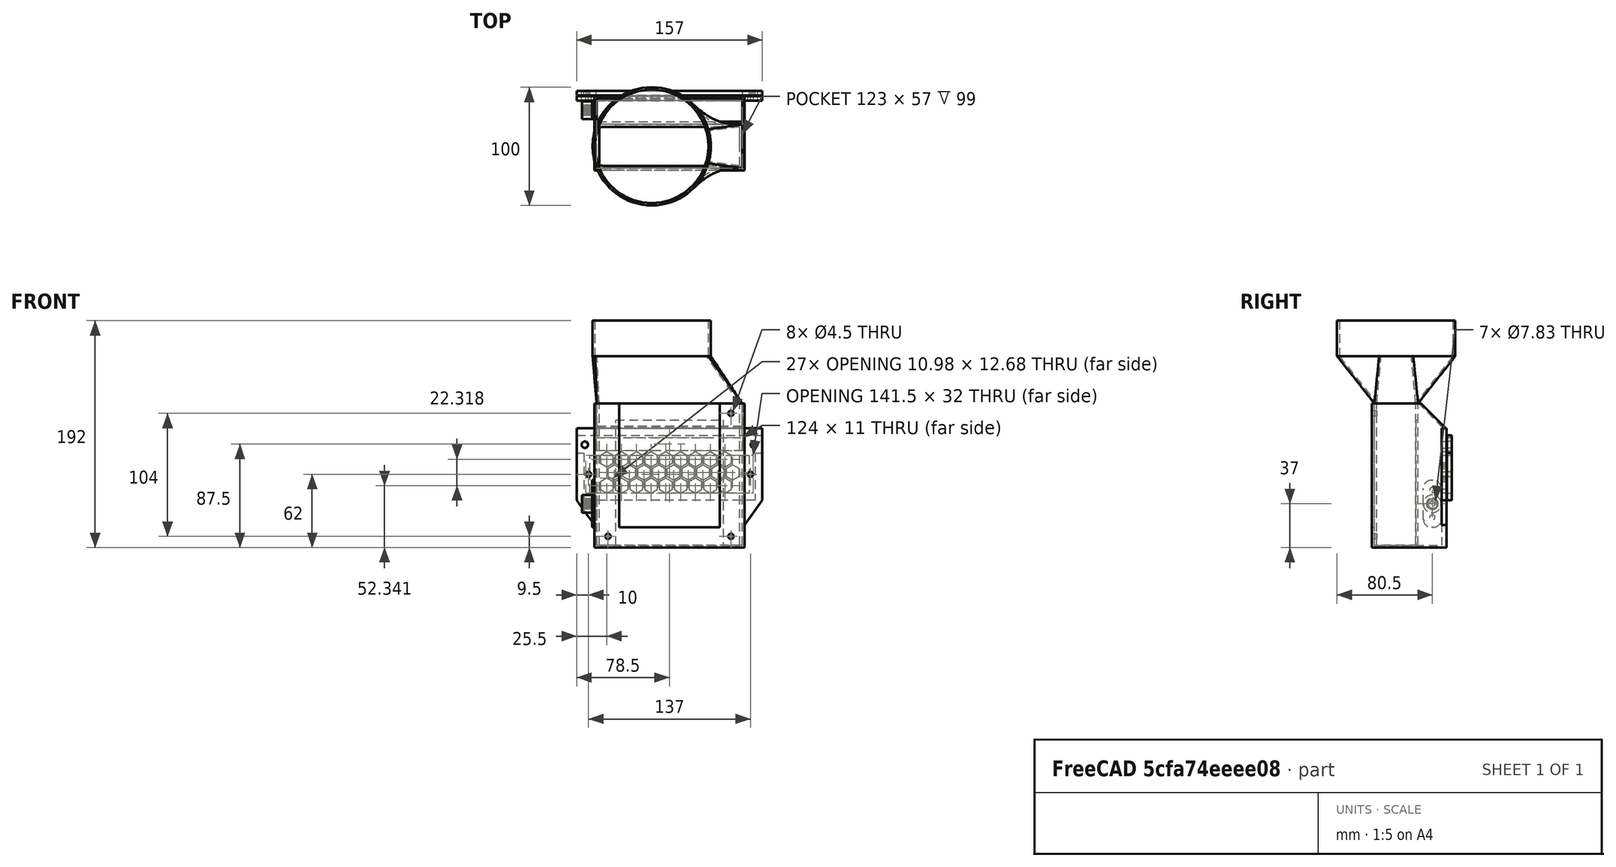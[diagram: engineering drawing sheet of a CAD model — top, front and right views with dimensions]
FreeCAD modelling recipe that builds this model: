
FCSTD DOCUMENT  (FreeCAD 1.0R39109 (Git))
Label: RadialExhaust
License: All rights reserved
LicenseURL: http://en.wikipedia.org/wiki/All_rights_reserved
objects: Sketcher::SketchObject×18, PartDesign::Pad×9, PartDesign::Pocket×8, PartDesign::Body×4, PartDesign::Fillet×2, Mesh::Feature×2, PartDesign::Hole×1, PartDesign::LinearPattern×1, PartDesign::AdditiveLoft×1
note: 105 computed .brp shape members not serialized (recipe doc carries the construction recipe); baked Part::Feature solids carry a one-line shape summary decoded from their .brp

FEATURE [Sketcher::SketchObject] Sketch  label="FanWallsSketch"
  ArcFitTolerance = 0
  AttachmentSupport = -> [XY_Plane]
  FullyConstrained = true
  MakeInternals = false
  MapMode = 5
  expr: Constraints[23] = .Constraints.brim
  sketch-geometry (10):
    g0: LineSegment StartX=-59.5 StartY=16.5 StartZ=0 EndX=-59.5 EndY=-16.5 EndZ=0
    g1: LineSegment StartX=-59.5 StartY=-16.5 StartZ=0 EndX=59.5 EndY=-16.5 EndZ=0
    g2: LineSegment StartX=59.5 StartY=-16.5 StartZ=0 EndX=59.5 EndY=16.5 EndZ=0
    g3: LineSegment StartX=59.5 StartY=16.5 StartZ=0 EndX=-59.5 EndY=16.5 EndZ=0
    g4: GeomPoint [constr] X=0 Y=0 Z=0
    g5: LineSegment StartX=-61.5 StartY=18.5 StartZ=0 EndX=-61.5 EndY=-18.5 EndZ=0
    g6: LineSegment StartX=-61.5 StartY=-18.5 StartZ=0 EndX=61.5 EndY=-18.5 EndZ=0
    g7: LineSegment StartX=61.5 StartY=-18.5 StartZ=0 EndX=61.5 EndY=18.5 EndZ=0
    g8: LineSegment StartX=61.5 StartY=18.5 StartZ=0 EndX=-61.5 EndY=18.5 EndZ=0
    g9: GeomPoint [constr] X=0 Y=0 Z=0
  constraints (24):
    c: Coincident(g0,g1)
    c: Coincident(g1,g2)
    c: Coincident(g2,g3)
    c: Coincident(g3,g0)
    c: Horizontal(g1)
    c: Horizontal(g3)
    c: Vertical(g0)
    c: Vertical(g2)
    c: Symmetric(g1,g0,g4)
    c: Coincident(g4,g-1)
    c: DistanceX(g3,g3) = 119  'width'
    c: DistanceY(g0,g0) = 33  'depth'
    c: Coincident(g5,g6)
    c: Coincident(g6,g7)
    c: Coincident(g7,g8)
    c: Coincident(g8,g5)
    c: Horizontal(g6)
    c: Horizontal(g8)
    c: Vertical(g5)
    c: Vertical(g7)
    c: Symmetric(g6,g5,g9)
    c: Coincident(g9,g4)
    c: DistanceX(g5,g0) = 2  'brim'
    c: DistanceY(g0,g5) = 2
FEATURE [PartDesign::Pad] Pad001  label="Walls"
  Direction = (0,0,1)
  Length = 120
  Length2 = 10
  Profile = -> Sketch
  ReferenceAxis = -> Sketch [N_Axis]
  Suppressed = false
  Type = 0
FEATURE [Sketcher::SketchObject] Sketch001  label="ExhaustPipeSketch"
  ArcFitTolerance = 0
  AttachmentOffset = pos=(0,0,160) rot=(0,0,1;0rad)
  AttachmentSupport = -> [XY_Plane]
  FullyConstrained = true
  MakeInternals = false
  MapMode = 5
  Placement = pos=(0,0,160) rot=(0,0,1;0rad)
  expr: Constraints[3] = .Constraints.outer_dia - 4 mm
  sketch-geometry (2):
    g0: Circle CenterX=-15 CenterY=0 CenterZ=0 NormalX=0 NormalY=0 NormalZ=1 AngleXU=0 Radius=50
    g1: Circle CenterX=-15 CenterY=0 CenterZ=0 NormalX=0 NormalY=0 NormalZ=1 AngleXU=0 Radius=48
  constraints (5):
    c: PointOnObject(g0,g-1)
    c: Coincident(g1,g0)
    c: Diameter(g0) = 100  'outer_dia'
    c: Diameter(g1) = 96
    c: DistanceX(g0,g-1) = 15
FEATURE [Sketcher::SketchObject] Sketch002  label="FanSkrewsSketch"
  ArcFitTolerance = 0
  AttachmentOffset = pos=(0,0,19) rot=(0,0,1;0rad)
  AttachmentSupport = -> [XZ_Plane]
  FullyConstrained = true
  MakeInternals = false
  MapMode = 5
  Placement = pos=(0,-19,4.2e-15) rot=(1,0,0;1.5708rad)
  expr: .Constraints.top_height_offset = 119 - 7.5
  expr: .Constraints.width_offset = <<FanWallsSketch>>.Constraints.width / 2 - 7.5 mm
  sketch-geometry (3):
    g0: Circle CenterX=-52 CenterY=7.5 CenterZ=0 NormalX=0 NormalY=0 NormalZ=1 AngleXU=0 Radius=2.25
    g1: Circle CenterX=52 CenterY=7.5 CenterZ=0 NormalX=0 NormalY=0 NormalZ=1 AngleXU=0 Radius=2.25
    g2: Circle CenterX=52 CenterY=111.5 CenterZ=0 NormalX=0 NormalY=0 NormalZ=1 AngleXU=0 Radius=2.25
  constraints (8):
    c: Equal(g0,g1)
    c: Equal(g0,g2)
    c: Diameter(g0) = 4.5  'dia'
    c: DistanceX(g0,g-1) = 52  'width_offset'
    c: Symmetric(g0,g1,g-2)
    c: DistanceY(g-1,g0) = 7.5  'height_offset'
    c: Vertical(g2,g1)
    c: DistanceY(g-1,g2) = 111.5  'top_height_offset'
FEATURE [Sketcher::SketchObject] Sketch003  label="FanInntakeSketch"
  ArcFitTolerance = 0
  AttachmentOffset = pos=(0,0,-16.5) rot=(0,0,1;0rad)
  AttachmentSupport = -> [XZ_Plane]
  FullyConstrained = true
  MakeInternals = false
  MapMode = 5
  Placement = pos=(0,16.5,-3.7e-15) rot=(1,0,0;1.5708rad)
  expr: .AttachmentOffset.Base.z = <<FanWallsSketch>>.Constraints.depth / -2
  expr: Constraints[10] = 59.5 - 14
  expr: Constraints[9] = 120 mm - 14 mm
  sketch-geometry (4):
    g0: LineSegment StartX=-45.5 StartY=106 StartZ=0 EndX=45.5 EndY=106 EndZ=0
    g1: LineSegment StartX=45.5 StartY=106 StartZ=0 EndX=45.5 EndY=0 EndZ=0
    g2: LineSegment StartX=45.5 StartY=0 StartZ=0 EndX=-45.5 EndY=0 EndZ=0
    g3: LineSegment StartX=-45.5 StartY=0 StartZ=0 EndX=-45.5 EndY=106 EndZ=0
  constraints (11):
    c: Coincident(g0,g1)
    c: Coincident(g1,g2)
    c: Coincident(g2,g3)
    c: Coincident(g3,g0)
    c: Horizontal(g2)
    c: Vertical(g1)
    c: Vertical(g3)
    c: PointOnObject(g1,g-1)
    c: Symmetric(g0,g0,g-2)
    c: DistanceY(g-1,g0) = 106
    c: DistanceX(g0,g-1) = 45.5
FEATURE [Sketcher::SketchObject] Sketch005  label="FloorSketch"
  ArcFitTolerance = 0
  AttachmentSupport = -> [XY_Plane001]
  FullyConstrained = true
  MakeInternals = false
  MapMode = 5
  expr: .Constraints.depth_offset = <<FanWallsSketch>>.Constraints.depth / 2 + 4 mm
  expr: .Constraints.width = <<FanWallsSketch>>.Constraints.width + 4 mm + 4 mm
  expr: Constraints[10] = <<FanWallsSketch>>.Constraints.depth / 2 + 4 mm + 20 mm + 2 mm
  sketch-geometry (4):
    g0: LineSegment StartX=-63.5 StartY=42.5 StartZ=0 EndX=63.5 EndY=42.5 EndZ=0
    g1: LineSegment StartX=63.5 StartY=42.5 StartZ=0 EndX=63.5 EndY=-20.5 EndZ=0
    g2: LineSegment StartX=63.5 StartY=-20.5 StartZ=0 EndX=-63.5 EndY=-20.5 EndZ=0
    g3: LineSegment StartX=-63.5 StartY=-20.5 StartZ=0 EndX=-63.5 EndY=42.5 EndZ=0
  constraints (12):
    c: Coincident(g0,g1)
    c: Coincident(g1,g2)
    c: Coincident(g2,g3)
    c: Coincident(g3,g0)
    c: Horizontal(g2)
    c: Vertical(g1)
    c: Vertical(g3)
    c: DistanceX(g0,g0) = 127  'width'
    c: Symmetric(g0,g0,g-2)
    c: DistanceY(g1,g-1) = 20.5  'depth_offset'
    c: DistanceY(g-1,g0) = 42.5
    c: DistanceY(g3,g3) = 63  'depth'
FEATURE [PartDesign::Pad] Pad002  label="FloorPad"
  Direction = (0,0,1)
  Length = 2
  Length2 = 10
  Profile = -> Sketch005
  ReferenceAxis = -> Sketch005 [N_Axis]
  Reversed = true
  Suppressed = false
  Type = 0
FEATURE [Sketcher::SketchObject] Sketch006  label="WallsSketch"
  ArcFitTolerance = 0
  AttachmentSupport = -> [XY_Plane001]
  FullyConstrained = true
  MakeInternals = false
  MapMode = 5
  expr: .Constraints.depth = <<FloorSketch>>.Constraints.depth
  expr: Constraints[8] = <<FloorSketch>>.Constraints.depth_offset
  expr: Constraints[9] = <<FloorSketch>>.Constraints.width
  sketch-geometry (8):
    g0: LineSegment StartX=-63.5 StartY=42.5 StartZ=0 EndX=63.5 EndY=42.5 EndZ=0
    g1: LineSegment StartX=63.5 StartY=42.5 StartZ=0 EndX=63.5 EndY=-20.5 EndZ=0
    g2: LineSegment StartX=63.5 StartY=-20.5 StartZ=0 EndX=-63.5 EndY=-20.5 EndZ=0
    g3: LineSegment StartX=-63.5 StartY=-20.5 StartZ=0 EndX=-63.5 EndY=42.5 EndZ=0
    g4: LineSegment StartX=-61.5 StartY=40.5 StartZ=0 EndX=61.5 EndY=40.5 EndZ=0
    g5: LineSegment StartX=61.5 StartY=40.5 StartZ=0 EndX=61.5 EndY=-18.5 EndZ=0
    g6: LineSegment StartX=61.5 StartY=-18.5 StartZ=0 EndX=-61.5 EndY=-18.5 EndZ=0
    g7: LineSegment StartX=-61.5 StartY=-18.5 StartZ=0 EndX=-61.5 EndY=40.5 EndZ=0
  constraints (24):
    c: Coincident(g0,g1)
    c: Coincident(g1,g2)
    c: Coincident(g2,g3)
    c: Coincident(g3,g0)
    c: Horizontal(g2)
    c: Vertical(g1)
    c: Vertical(g3)
    c: Symmetric(g0,g0,g-2)
    c: DistanceY(g2,g-1) = 20.5
    c: DistanceX(g0,g0) = 127
    c: DistanceY(g1,g1) = 63  'depth'
    c: Coincident(g4,g5)
    c: Coincident(g5,g6)
    c: Coincident(g6,g7)
    c: Coincident(g7,g4)
    c: Horizontal(g4)
    c: Horizontal(g6)
    c: Vertical(g5)
    c: Vertical(g7)
    c: DistanceX(g0,g4) = 2
    c: DistanceY(g4,g0) = 2
    c: DistanceY(g1,g5) = 2
    c: DistanceX(g5,g1) = 2
    c: DistanceX(g4,g4) = 123
FEATURE [PartDesign::Pad] Pad003  label="WallsPad"
  BaseFeature = -> Pad002
  Direction = (0,0,1)
  Length = 120
  Length2 = 10
  Profile = -> Sketch006
  ReferenceAxis = -> Sketch006 [N_Axis]
  Suppressed = false
  Type = 0
FEATURE [Sketcher::SketchObject] Sketch007  label="CornerCutSketch"
  ArcFitTolerance = 0
  AttachmentSupport = -> [YZ_Plane001]
  FullyConstrained = true
  MakeInternals = false
  MapMode = 5
  Placement = pos=(0,0,0) rot=(0.57735,0.57735,0.57735;2.0944rad)
  expr: .Constraints.corner_width = <<WallsSketch>>.Constraints.depth - 4 mm - 37 mm
  expr: Constraints[8] = .Constraints.corner_width
  sketch-geometry (3):
    g0: LineSegment StartX=43 StartY=120 StartZ=0 EndX=21 EndY=120 EndZ=0
    g1: LineSegment StartX=21 StartY=120 StartZ=0 EndX=43 EndY=98 EndZ=0
    g2: LineSegment StartX=43 StartY=98 StartZ=0 EndX=43 EndY=120 EndZ=0
  constraints (9):
    c: Horizontal(g0)
    c: Coincident(g0,g1)
    c: Coincident(g1,g2)
    c: Coincident(g2,g0)
    c: Vertical(g2)
    c: DistanceX(g-1,g0) = 43  'corner_width_offset'
    c: DistanceY(g-1,g0) = 120  'corner_height_offset'
    c: DistanceX(g0,g0) = 22  'corner_width'
    c: DistanceY(g2,g2) = 22
FEATURE [PartDesign::Pocket] Pocket003  label="CornerCut"
  BaseFeature = -> Pad003
  Direction = (-1,0,0)
  Length = 150
  Length2 = 5
  Midplane = true
  Profile = -> Sketch007
  ReferenceAxis = -> Sketch007 [N_Axis]
  Suppressed = false
  Type = 0
FEATURE [Sketcher::SketchObject] Sketch008  label="CornerPadSketch"
  ArcFitTolerance = 0
  AttachmentSupport = -> [YZ_Plane001]
  FullyConstrained = true
  MakeInternals = false
  MapMode = 5
  Placement = pos=(0,0,0) rot=(0.57735,0.57735,0.57735;2.0944rad)
  expr: Constraints[10] = <<CornerCutSketch>>.Constraints.corner_height_offset
  expr: Constraints[11] = <<CornerCutSketch>>.Constraints.corner_width_offset
  expr: Constraints[12] = <<CornerCutSketch>>.Constraints.corner_width
  expr: Constraints[13] = <<CornerCutSketch>>.Constraints.corner_width
  sketch-geometry (5):
    g0: LineSegment StartX=21 StartY=120 StartZ=0 EndX=42.5 EndY=98 EndZ=0
    g1: LineSegment StartX=42.5 StartY=98 StartZ=0 EndX=42.5 EndY=96 EndZ=0
    g2: LineSegment StartX=42.5 StartY=96 StartZ=0 EndX=19 EndY=120 EndZ=0
    g3: LineSegment StartX=19 StartY=120 StartZ=0 EndX=21 EndY=120 EndZ=0
    g4: GeomPoint [constr] X=43 Y=120 Z=0
  constraints (14):
    c: Coincident(g0,g1)
    c: Vertical(g1)
    c: Coincident(g1,g2)
    c: Coincident(g2,g3)
    c: Coincident(g3,g0)
    c: Horizontal(g3)
    c: DistanceY(g-1,g0) = 120
    c: DistanceX(g-1,g0) = 42.5
    c: DistanceX(g3,g3) = 2
    c: DistanceY(g1,g1) = 2
    c: DistanceY(g-1,g4) = 120
    c: DistanceX(g-1,g4) = 43
    c: DistanceX(g0,g4) = 22
    c: DistanceY(g0,g4) = 22
FEATURE [PartDesign::Pad] Pad004  label="CornerPad"
  BaseFeature = -> Pocket003
  Direction = (1,0,0)
  Length = 127
  Length2 = 10
  Midplane = true
  Profile = -> Sketch008
  ReferenceAxis = -> Sketch008 [N_Axis]
  Suppressed = false
  Type = 0
FEATURE [Sketcher::SketchObject] Sketch010  label="ConnectorSketch"
  ArcFitTolerance = 0
  AttachmentOffset = pos=(0,0,-42.5) rot=(0,0,1;0rad)
  AttachmentSupport = -> [XZ_Plane001]
  FullyConstrained = true
  MakeInternals = false
  MapMode = 5
  Placement = pos=(0,42.5,-9.4e-15) rot=(1,0,0;1.5708rad)
  sketch-geometry (12):
    g0: LineSegment StartX=-78.5 StartY=99 StartZ=0 EndX=78.5 EndY=99 EndZ=0
    g1: LineSegment StartX=78.5 StartY=99 StartZ=0 EndX=78.5 EndY=38 EndZ=0
    g2: LineSegment StartX=78.5 StartY=38 StartZ=0 EndX=62 EndY=15 EndZ=0
    g3: LineSegment StartX=-78.5 StartY=99 StartZ=0 EndX=-78.5 EndY=38 EndZ=0
    g4: LineSegment StartX=-78.5 StartY=38 StartZ=0 EndX=-62 EndY=15 EndZ=0
    g5: Circle CenterX=-68.5 CenterY=60 CenterZ=0 NormalX=0 NormalY=0 NormalZ=1 AngleXU=0 Radius=2.25
    g6: Circle CenterX=68.5 CenterY=60 CenterZ=0 NormalX=0 NormalY=0 NormalZ=1 AngleXU=0 Radius=2.25
    g7: Circle CenterX=-71.5 CenterY=85 CenterZ=0 NormalX=0 NormalY=0 NormalZ=1 AngleXU=0 Radius=2.75
    g8: Circle CenterX=71.5 CenterY=85 CenterZ=0 NormalX=0 NormalY=0 NormalZ=1 AngleXU=0 Radius=2.75
    g9: LineSegment StartX=-62 StartY=15 StartZ=0 EndX=-62 EndY=0 EndZ=0
    g10: LineSegment StartX=62 StartY=15 StartZ=0 EndX=62 EndY=0 EndZ=0
    g11: LineSegment StartX=62 StartY=0 StartZ=0 EndX=-62 EndY=0 EndZ=0
  constraints (31):
    c: DistanceX(g0,g0) = 157
    c: Symmetric(g0,g0,g-2)
    c: DistanceY(g-1,g4) = 15
    c: Coincident(g0,g1)
    c: Vertical(g1)
    c: Coincident(g1,g2)
    c: DistanceY(g2,g0) = 84
    c: Coincident(g0,g3)
    c: Coincident(g3,g4)
    c: Symmetric(g4,g2,g-2)
    c: DistanceX(g4,g2) = 124
    c: Symmetric(g3,g1,g-2)
    c: Diameter(g5) = 4.5
    c: Diameter(g6) = 4.5
    c: Symmetric(g5,g6,g-2)
    c: DistanceX(g5,g6) = 137
    c: DistanceY(g-1,g5) = 60
    c: Symmetric(g7,g8,g-2)
    c: Diameter(g7) = 5.5
    c: Diameter(g8) = 5.5
    c: DistanceX(g7,g5) = 3
    c: DistanceY(g6,g8) = 25
    c: DistanceY(g1,g1) = 61
    c: Coincident(g9,g4)
    c: PointOnObject(g9,g-1)
    c: Vertical(g9)
    c: Coincident(g10,g2)
    c: PointOnObject(g10,g-1)
    c: Vertical(g10)
    c: Coincident(g11,g10)
    c: Coincident(g11,g9)
FEATURE [Sketcher::SketchObject] Sketch011  label="SkrewHoleSketch"
  ArcFitTolerance = 0
  AttachmentOffset = pos=(0,0,21) rot=(0,0,1;0rad)
  AttachmentSupport = -> [XZ_Plane001]
  FullyConstrained = true
  MakeInternals = false
  MapMode = 5
  Placement = pos=(0,-21,4.7e-15) rot=(1,0,0;1.5708rad)
  expr: Constraints[2] = <<FanSkrewsSketch>>.Constraints.dia
  expr: Constraints[3] = <<FanSkrewsSketch>>.Constraints.height_offset
  expr: Constraints[6] = <<FanSkrewsSketch>>.Constraints.top_height_offset
  expr: Constraints[7] = <<FanSkrewsSketch>>.Constraints.width_offset
  sketch-geometry (3):
    g0: Circle CenterX=52 CenterY=111.5 CenterZ=0 NormalX=0 NormalY=0 NormalZ=1 AngleXU=0 Radius=2.25
    g1: Circle CenterX=52 CenterY=7.5 CenterZ=0 NormalX=0 NormalY=0 NormalZ=1 AngleXU=0 Radius=2.25
    g2: Circle CenterX=-52 CenterY=7.5 CenterZ=0 NormalX=0 NormalY=0 NormalZ=1 AngleXU=0 Radius=2.25
  constraints (8):
    c: Equal(g2,g1)
    c: Equal(g2,g0)
    c: Diameter(g2) = 4.5
    c: DistanceY(g-1,g2) = 7.5
    c: Symmetric(g1,g2,g-2)
    c: Vertical(g0,g1)
    c: DistanceY(g-1,g0) = 111.5
    c: DistanceX(g2,g-1) = 52
FEATURE [Sketcher::SketchObject] Sketch012  label="SkrewHolesSketch"
  ArcFitTolerance = 0
  AttachmentOffset = pos=(0,0,-43) rot=(0,0,1;0rad)
  AttachmentSupport = -> [XZ_Plane003]
  FullyConstrained = true
  MakeInternals = false
  MapMode = 5
  Placement = pos=(0,43,-9.5e-15) rot=(1,0,0;1.5708rad)
  sketch-geometry (16):
    g0: LineSegment StartX=-78.5 StartY=93 StartZ=0 EndX=78.5 EndY=93 EndZ=0
    g1: LineSegment StartX=72.5 StartY=38 StartZ=0 EndX=-72.5 EndY=38 EndZ=0
    g2: Circle CenterX=-71.75 CenterY=85 CenterZ=0 NormalX=0 NormalY=0 NormalZ=1 AngleXU=0 Radius=2.75
    g3: Circle CenterX=-68.5 CenterY=60 CenterZ=0 NormalX=0 NormalY=0 NormalZ=1 AngleXU=0 Radius=2.25
    g4: Circle CenterX=71.75 CenterY=85 CenterZ=0 NormalX=0 NormalY=0 NormalZ=1 AngleXU=0 Radius=2.75
    g5: Circle CenterX=68.5 CenterY=60 CenterZ=0 NormalX=0 NormalY=0 NormalZ=1 AngleXU=0 Radius=2.25
    g6: LineSegment StartX=-78.5 StartY=93 StartZ=0 EndX=-78.5 EndY=78 EndZ=0
    g7: LineSegment StartX=-78.5 StartY=78 StartZ=0 EndX=-72.5 EndY=78 EndZ=0
    g8: LineSegment StartX=-72.5 StartY=78 StartZ=0 EndX=-72.5 EndY=38 EndZ=0
    g9: LineSegment StartX=78.5 StartY=93 StartZ=0 EndX=78.5 EndY=78 EndZ=0
    g10: LineSegment StartX=72.5 StartY=78 StartZ=0 EndX=78.5 EndY=78 EndZ=0
    g11: LineSegment StartX=72.5 StartY=78 StartZ=0 EndX=72.5 EndY=38 EndZ=0
    g12: LineSegment StartX=-62 StartY=91 StartZ=0 EndX=62 EndY=91 EndZ=0
    g13: LineSegment StartX=62 StartY=91 StartZ=0 EndX=62 EndY=80 EndZ=0
    g14: LineSegment StartX=62 StartY=80 StartZ=0 EndX=-62 EndY=80 EndZ=0
    g15: LineSegment StartX=-62 StartY=80 StartZ=0 EndX=-62 EndY=91 EndZ=0
  constraints (43):
    c: Horizontal(g1)
    c: Symmetric(g0,g0,g-2)
    c: DistanceY(g-1,g1) = 38
    c: DistanceX(g0,g0) = 157
    c: DistanceY(g1,g0) = 55
    c: Diameter(g2) = 5.5
    c: Diameter(g4) = 5.5
    c: Diameter(g5) = 4.5
    c: Diameter(g3) = 4.5
    c: DistanceX(g3,g5) = 137
    c: DistanceX(g2,g4) = 143.5
    c: Symmetric(g4,g2,g-2)
    c: Symmetric(g3,g5,g-2)
    c: DistanceY(g3,g2) = 25
    c: DistanceY(g-1,g3) = 60
    c: Coincident(g6,g0)
    c: Vertical(g6)
    c: Coincident(g7,g6)
    c: Coincident(g8,g7)
    c: Coincident(g8,g1)
    c: Vertical(g8)
    c: Coincident(g9,g0)
    c: Vertical(g9)
    c: Coincident(g10,g9)
    c: Coincident(g11,g10)
    c: Coincident(g11,g1)
    c: Vertical(g11)
    c: Horizontal(g6,g7)
    c: Horizontal(g10,g9)
    c: DistanceX(g7,g10) = 145
    c: Symmetric(g7,g10,g-2)
    c: DistanceY(g6,g6) = 15
    c: Coincident(g12,g13)
    c: Coincident(g13,g14)
    c: Coincident(g14,g15)
    c: Coincident(g15,g12)
    c: Horizontal(g14)
    c: Vertical(g13)
    c: Vertical(g15)
    c: DistanceY(g12,g0) = 2
    c: DistanceY(g6,g14) = 2
    c: Symmetric(g12,g12,g-2)
    c: DistanceX(g12,g12) = 124
FEATURE [PartDesign::Pad] Pad006  label="SkrewHoles"
  Direction = (0,-1,2e-16)
  Length = 4
  Length2 = 10
  Placement = pos=(0,0,0) rot=(1,0,0;1.5708rad)
  Profile = -> Sketch012
  ReferenceAxis = -> Sketch012 [N_Axis]
  Reversed = true
  Suppressed = false
  Type = 0
FEATURE [Sketcher::SketchObject] Sketch013
  ArcFitTolerance = 0
  AttachmentOffset = pos=(0,0,-43) rot=(0,0,1;0rad)
  AttachmentSupport = -> [XZ_Plane003]
  FullyConstrained = true
  MakeInternals = false
  MapMode = 5
  Placement = pos=(0,43,-9.5e-15) rot=(1,0,0;1.5708rad)
  expr: Constraints[10] = 60 - 32 / 2
  sketch-geometry (4):
    g0: LineSegment StartX=-67.25 StartY=76 StartZ=0 EndX=67.25 EndY=76 EndZ=0
    g1: LineSegment StartX=67.25 StartY=76 StartZ=0 EndX=67.25 EndY=44 EndZ=0
    g2: LineSegment StartX=67.25 StartY=44 StartZ=0 EndX=-67.25 EndY=44 EndZ=0
    g3: LineSegment StartX=-67.25 StartY=44 StartZ=0 EndX=-67.25 EndY=76 EndZ=0
  constraints (11):
    c: Coincident(g0,g1)
    c: Coincident(g1,g2)
    c: Coincident(g2,g3)
    c: Coincident(g3,g0)
    c: Horizontal(g2)
    c: Vertical(g1)
    c: Vertical(g3)
    c: Symmetric(g0,g0,g-2)
    c: DistanceX(g0,g0) = 134.5
    c: DistanceY(g1,g1) = 32
    c: DistanceY(g-1,g2) = 44
FEATURE [PartDesign::Pocket] Pocket006
  BaseFeature = -> Pad006
  Direction = (0,1,-2e-16)
  Length = 5
  Length2 = 5
  Placement = pos=(0,0,0) rot=(1,0,0;1.5708rad)
  Profile = -> Sketch013
  ReferenceAxis = -> Sketch013 [N_Axis]
  Suppressed = false
  Type = 0
FEATURE [PartDesign::Body] Body002  label="ConnectorTap"
  AllowCompound = false
  Group = -> [Sketch012,Pad006,Sketch013,Pocket006]
  Origin = -> Origin003
  Tip = -> Pocket006
FEATURE [Sketcher::SketchObject] Sketch014  label="BowdenSkrewSketch"
  ArcFitTolerance = 0
  AttachmentOffset = pos=(0,0,-64) rot=(0,0,1;0rad)
  AttachmentSupport = -> [YZ_Plane001]
  FullyConstrained = true
  MakeInternals = false
  MapMode = 5
  Placement = pos=(-64,0,0) rot=(0.57735,0.57735,0.57735;2.0944rad)
  expr: .Constraints.depth_offset = <<FanWallsSketch>>.Constraints.depth / 2 + 10 mm + 2 mm + 2 mm
  sketch-geometry (3):
    g0: Circle CenterX=30.5 CenterY=46.5 CenterZ=0 NormalX=0 NormalY=0 NormalZ=1 AngleXU=0 Radius=2.25
    g1: Circle CenterX=30.5 CenterY=35 CenterZ=0 NormalX=0 NormalY=0 NormalZ=1 AngleXU=0 Radius=2.25
    g2: Circle CenterX=30.5 CenterY=23.5 CenterZ=0 NormalX=0 NormalY=0 NormalZ=1 AngleXU=0 Radius=2.25
  constraints (9):
    c: Equal(g2,g1)
    c: Equal(g2,g0)
    c: Diameter(g2) = 4.5
    c: Vertical(g0,g1)
    c: Vertical(g1,g2)
    c: DistanceX(g-1,g0) = 30.5  'depth_offset'
    c: DistanceY(g1,g0) = 11.5  'hole_buffer'
    c: DistanceY(g2,g1) = 11.5
    c: DistanceY(g-1,g1) = 35  'height_offset'
FEATURE [Sketcher::SketchObject] Sketch015  label="BowdenBaseSketch"
  ArcFitTolerance = 0
  AttachmentOffset = pos=(0,0,-64) rot=(0,0,1;0rad)
  AttachmentSupport = -> [YZ_Plane004]
  FullyConstrained = true
  MakeInternals = false
  MapMode = 5
  Placement = pos=(-64,0,0) rot=(0.57735,0.57735,0.57735;2.0944rad)
  expr: Constraints[10] = <<BowdenSkrewSketch>>.Constraints.depth_offset - 7.5 mm
  expr: Constraints[11] = <<BowdenSkrewSketch>>.Constraints.height_offset - 20 mm
  expr: Constraints[14] = 4.5
  expr: Constraints[17] = <<BowdenSkrewSketch>>.Constraints.hole_buffer
  expr: Constraints[18] = <<BowdenSkrewSketch>>.Constraints.hole_buffer
  expr: Constraints[19] = <<BowdenSkrewSketch>>.Constraints.height_offset
  expr: Constraints[20] = <<BowdenSkrewSketch>>.Constraints.depth_offset
  sketch-geometry (7):
    g0: LineSegment StartX=23 StartY=55 StartZ=0 EndX=38 EndY=55 EndZ=0
    g1: LineSegment StartX=38 StartY=55 StartZ=0 EndX=38 EndY=15 EndZ=0
    g2: LineSegment StartX=38 StartY=15 StartZ=0 EndX=23 EndY=15 EndZ=0
    g3: LineSegment StartX=23 StartY=15 StartZ=0 EndX=23 EndY=55 EndZ=0
    g4: Circle CenterX=30.5 CenterY=46.5 CenterZ=0 NormalX=0 NormalY=0 NormalZ=1 AngleXU=0 Radius=2.25
    g5: Circle CenterX=30.5 CenterY=35 CenterZ=0 NormalX=0 NormalY=0 NormalZ=1 AngleXU=0 Radius=2.25
    g6: Circle CenterX=30.5 CenterY=23.5 CenterZ=0 NormalX=0 NormalY=0 NormalZ=1 AngleXU=0 Radius=2.25
  constraints (21):
    c: Coincident(g0,g1)
    c: Coincident(g1,g2)
    c: Coincident(g2,g3)
    c: Coincident(g3,g0)
    c: Horizontal(g0)
    c: Horizontal(g2)
    c: Vertical(g1)
    c: Vertical(g3)
    c: DistanceY(g1,g1) = 40
    c: DistanceX(g0,g0) = 15
    c: DistanceX(g-1,g0) = 23
    c: DistanceY(g-1,g2) = 15
    c: Equal(g4,g5)
    c: Equal(g4,g6)
    c: Diameter(g4) = 4.5
    c: Vertical(g6,g5)
    c: Vertical(g5,g4)
    c: DistanceY(g5,g4) = 11.5
    c: DistanceY(g6,g5) = 11.5
    c: DistanceY(g-1,g5) = 35
    c: DistanceX(g-1,g5) = 30.5
FEATURE [PartDesign::Pad] Pad007  label="BowdenBase"
  Direction = (1,0,0)
  Length = 1.5
  Length2 = 10
  Placement = pos=(0,0,0) rot=(1,1,1;2.0944rad)
  Profile = -> Sketch015
  ReferenceAxis = -> Sketch015 [N_Axis]
  Reversed = true
  Suppressed = false
  Type = 0
FEATURE [Sketcher::SketchObject] Sketch016  label="BowdenBrimSketch"
  ArcFitTolerance = 0
  AttachmentOffset = pos=(0,0,-64) rot=(0,0,1;0rad)
  AttachmentSupport = -> [YZ_Plane004]
  FullyConstrained = true
  MakeInternals = false
  MapMode = 5
  Placement = pos=(-64,0,0) rot=(0.57735,0.57735,0.57735;2.0944rad)
  expr: Constraints[1] = <<BowdenSkrewSketch>>.Constraints.height_offset
  expr: Constraints[2] = <<BowdenSkrewSketch>>.Constraints.depth_offset
  sketch-geometry (1):
    g0: Circle CenterX=30.5 CenterY=35 CenterZ=0 NormalX=0 NormalY=0 NormalZ=1 AngleXU=0 Radius=7.5
  constraints (3):
    c: Diameter(g0) = 15
    c: DistanceY(g-1,g0) = 35
    c: DistanceX(g-1,g0) = 30.5
FEATURE [PartDesign::Pad] Pad008  label="BowdenBrim"
  BaseFeature = -> Pad007
  Direction = (1,0,0)
  Length = 10
  Length2 = 10
  Placement = pos=(0,0,0) rot=(1,1,1;2.0944rad)
  Profile = -> Sketch016
  ReferenceAxis = -> Sketch016 [N_Axis]
  Reversed = true
  Suppressed = false
  Type = 0
FEATURE [Sketcher::SketchObject] Sketch018  label="BowdenSkrewSketch001"
  ArcFitTolerance = 0
  AttachmentOffset = pos=(0,0,-74) rot=(0,0,1;0rad)
  AttachmentSupport = -> [YZ_Plane004]
  FullyConstrained = true
  MakeInternals = false
  MapMode = 5
  Placement = pos=(-74,0,0) rot=(0.57735,0.57735,0.57735;2.0944rad)
  expr: Constraints[1] = <<BowdenSkrewSketch>>.Constraints.depth_offset
  expr: Constraints[2] = <<BowdenSkrewSketch>>.Constraints.height_offset
  sketch-geometry (1):
    g0: Circle CenterX=30.5 CenterY=35 CenterZ=0 NormalX=0 NormalY=0 NormalZ=1 AngleXU=0 Radius=4.5
  constraints (3):
    c: Diameter(g0) = 9
    c: DistanceX(g-1,g0) = 30.5
    c: DistanceY(g-1,g0) = 35
FEATURE [PartDesign::Hole] Hole  label="BowdenSkrewHole"
  BaseFeature = -> Pad008
  CustomThreadClearance = 0
  Depth = 15
  DepthType = 0
  Diameter = 7.828
  DrillForDepth = false
  DrillPoint = 1
  DrillPointAngle = 118
  HoleCutCountersinkAngle = 90
  HoleCutCustomValues = false
  HoleCutDepth = 0
  HoleCutDiameter = 10
  HoleCutType = 2
  ModelThread = true
  Placement = pos=(0,0,0) rot=(1,1,1;2.0944rad)
  Profile = -> Sketch018
  Reversed = true
  Suppressed = false
  Tapered = false
  TaperedAngle = 90
  ThreadClass = 0
  ThreadDepth = 15
  ThreadDepthType = 0
  ThreadDirection = 0
  ThreadFit = 0
  ThreadSize = 17
  ThreadType = 1
  Threaded = true
  UseCustomThreadClearance = false
FEATURE [PartDesign::Pad] Pad009  label="Connector"
  BaseFeature = -> Pad004
  Direction = (0,-1,2e-16)
  Length = 4
  Length2 = 10
  Profile = -> Sketch010
  ReferenceAxis = -> Sketch010 [N_Axis]
  Suppressed = false
  Type = 0
FEATURE [PartDesign::Pocket] Pocket005  label="Skrewhole"
  BaseFeature = -> Pad009
  Direction = (0,1,-2e-16)
  Length = 4
  Length2 = 5
  Profile = -> Sketch011
  ReferenceAxis = -> Sketch011 [N_Axis]
  Suppressed = false
  Type = 0
FEATURE [PartDesign::Pocket] Pocket007  label="BowdenSkrew"
  BaseFeature = -> Pocket005
  Direction = (-1,0,0)
  Length = 5
  Length2 = 5
  Midplane = true
  Profile = -> Sketch014
  ReferenceAxis = -> Sketch014 [N_Axis]
  Suppressed = false
  Type = 0
FEATURE [PartDesign::Fillet] Fillet
  Base = -> Pocket007
  BaseFeature = -> Pocket007
  Radius = 1
  SupportTransform = false
  Suppressed = false
  UseAllEdges = false
FEATURE [PartDesign::Fillet] Fillet001  label="BaseFillet"
  Base = -> Hole [Edge17,Edge19,Edge2,Edge1]
  BaseFeature = -> Hole
  Placement = pos=(0,0,0) rot=(1,1,1;2.0944rad)
  Radius = 7
  SupportTransform = false
  Suppressed = false
  UseAllEdges = false
FEATURE [PartDesign::Body] Body003  label="BowdenAttachment"
  AllowCompound = false
  Group = -> [Sketch015,Pad007,Sketch016,Pad008,Sketch018,Hole,Fillet001]
  Origin = -> Origin004
  Tip = -> Fillet001
FEATURE [Sketcher::SketchObject] Sketch021  label="HexSketch"
  ArcFitTolerance = 0
  AttachmentOffset = pos=(0,0,-43) rot=(0,0,1;0rad)
  AttachmentSupport = -> [XZ_Plane001]
  FullyConstrained = true
  MakeInternals = false
  MapMode = 5
  Placement = pos=(0,43,-9.5e-15) rot=(1,0,0;1.5708rad)
  sketch-geometry (31):
    g0: LineSegment StartX=-58.4915 StartY=69.4885 StartZ=0 EndX=-53 EndY=66.318 EndZ=0
    g1: LineSegment StartX=-53 StartY=66.318 StartZ=0 EndX=-47.5085 EndY=69.4885 EndZ=0
    g2: LineSegment StartX=-47.5085 StartY=69.4885 StartZ=0 EndX=-47.5085 EndY=75.8295 EndZ=0
    g3: LineSegment StartX=-47.5085 StartY=75.8295 StartZ=0 EndX=-53 EndY=79 EndZ=0
    g4: LineSegment StartX=-53 StartY=79 StartZ=0 EndX=-58.4915 EndY=75.8295 EndZ=0
    g5: LineSegment StartX=-58.4915 StartY=75.8295 StartZ=0 EndX=-58.4915 EndY=69.4885 EndZ=0
    g6: Circle [constr] CenterX=-53 CenterY=72.659 CenterZ=0 NormalX=0 NormalY=0 NormalZ=1 AngleXU=0 Radius=6.34102
    g7: LineSegment [constr] StartX=-62 StartY=79 StartZ=0 EndX=62 EndY=79 EndZ=0
    g8: LineSegment [constr] StartX=62 StartY=79 StartZ=0 EndX=62 EndY=44 EndZ=0
    g9: LineSegment [constr] StartX=62 StartY=44 StartZ=0 EndX=-62 EndY=44 EndZ=0
    g10: LineSegment [constr] StartX=-62 StartY=44 StartZ=0 EndX=-62 EndY=79 EndZ=0
    g11: LineSegment StartX=-46.5574 StartY=55.159 StartZ=0 EndX=-41.0659 EndY=58.3295 EndZ=0
    g12: LineSegment StartX=-41.0659 StartY=58.3295 StartZ=0 EndX=-41.0659 EndY=64.6705 EndZ=0
    g13: LineSegment StartX=-41.0659 StartY=64.6705 StartZ=0 EndX=-46.5574 EndY=67.841 EndZ=0
    g14: LineSegment StartX=-46.5574 StartY=67.841 StartZ=0 EndX=-52.0488 EndY=64.6705 EndZ=0
    g15: LineSegment StartX=-52.0488 StartY=64.6705 StartZ=0 EndX=-52.0488 EndY=58.3295 EndZ=0
    g16: LineSegment StartX=-52.0488 StartY=58.3295 StartZ=0 EndX=-46.5574 EndY=55.159 EndZ=0
    g17: Circle [constr] CenterX=-46.5574 CenterY=61.5 CenterZ=0 NormalX=0 NormalY=0 NormalZ=1 AngleXU=0 Radius=6.34102
    g18: LineSegment StartX=-47.5085 StartY=47.1705 StartZ=0 EndX=-47.5085 EndY=53.5115 EndZ=0
    g19: LineSegment StartX=-47.5085 StartY=53.5115 StartZ=0 EndX=-53 EndY=56.682 EndZ=0
    g20: LineSegment StartX=-53 StartY=56.682 StartZ=0 EndX=-58.4915 EndY=53.5115 EndZ=0
    g21: LineSegment StartX=-58.4915 StartY=53.5115 StartZ=0 EndX=-58.4915 EndY=47.1705 EndZ=0
    g22: LineSegment StartX=-58.4915 StartY=47.1705 StartZ=0 EndX=-53 EndY=44 EndZ=0
    g23: LineSegment StartX=-53 StartY=44 StartZ=0 EndX=-47.5085 EndY=47.1705 EndZ=0
    g24: Circle [constr] CenterX=-53 CenterY=50.341 CenterZ=0 NormalX=0 NormalY=0 NormalZ=1 AngleXU=0 Radius=6.34102
    g25: LineSegment [constr] StartX=-47.5085 StartY=69.4885 StartZ=0 EndX=-46.5574 EndY=67.841 EndZ=0
    g26: LineSegment [constr] StartX=-46.5574 StartY=67.841 StartZ=0 EndX=-45.6062 EndY=69.4885 EndZ=0
    g27: LineSegment [constr] StartX=-45.6062 StartY=69.4885 StartZ=0 EndX=-47.5085 EndY=69.4885 EndZ=0
    g28: LineSegment [constr] StartX=-53 StartY=56.682 StartZ=0 EndX=-52.0488 EndY=58.3295 EndZ=0
    g29: LineSegment [constr] StartX=-52.0488 StartY=58.3295 StartZ=0 EndX=-53.9512 EndY=58.3295 EndZ=0
    g30: LineSegment [constr] StartX=-53.9512 StartY=58.3295 StartZ=0 EndX=-53 EndY=56.682 EndZ=0
  constraints (77):
    c: Coincident(g0,g1)
    c: Coincident(g1,g2)
    c: Coincident(g2,g3)
    c: Coincident(g3,g4)
    c: Coincident(g4,g5)
    c: Coincident(g5,g0)
    c: Equal(g0, g1-g5) x5
    c: PointOnObject(g0,g6)
    c: PointOnObject(g1,g6)
    c: PointOnObject(g2,g6)
    c: PointOnObject(g3,g6)
    c: PointOnObject(g4,g6)
    c: PointOnObject(g5,g6)
    c: Vertical(g3,g0)
    c: Coincident(g7,g8)
    c: Coincident(g8,g9)
    c: Coincident(g9,g10)
    c: Coincident(g10,g7)
    c: Horizontal(g9)
    c: Vertical(g8)
    c: Vertical(g10)
    c: Symmetric(g7,g7,g-2)
    c: DistanceX(g7,g7) = 124
    c: DistanceY(g8,g8) = 35
    c: DistanceY(g-1,g9) = 44
    c: Coincident(g11,g12)
    c: Coincident(g12,g13)
    c: Coincident(g13,g14)
    c: Coincident(g14,g15)
    c: Coincident(g15,g16)
    c: Coincident(g16,g11)
    c: Equal(g11, g12-g16) x5
    c: PointOnObject(g11,g17)
    c: PointOnObject(g12,g17)
    c: PointOnObject(g13,g17)
    c: PointOnObject(g14,g17)
    c: PointOnObject(g15,g17)
    c: PointOnObject(g16,g17)
    c: Coincident(g18,g19)
    c: Coincident(g19,g20)
    c: Coincident(g20,g21)
    c: Coincident(g21,g22)
    c: Coincident(g22,g23)
    c: Coincident(g23,g18)
    c: Equal(g18, g19-g23) x5
    c: PointOnObject(g18,g24)
    c: PointOnObject(g19,g24)
    c: PointOnObject(g20,g24)
    c: PointOnObject(g21,g24)
    c: PointOnObject(g22,g24)
    c: PointOnObject(g23,g24)
    c: Coincident(g25,g1)
    c: Coincident(g25,g13)
    c: Coincident(g26,g13)
    c: Coincident(g27,g26)
    c: Coincident(g27,g1)
    c: Horizontal(g27)
    c: Equal(g17,g6)
    c: Equal(g26,g27)
    c: Equal(g27,g25)
    c: Coincident(g28,g19)
    c: Coincident(g28,g15)
    c: Coincident(g29,g15)
    c: Horizontal(g29)
    c: Coincident(g30,g29)
    c: Coincident(g30,g19)
    c: Equal(g29,g28)
    c: Equal(g28,g30)
    c: Equal(g24,g17)
    c: Vertical(g11,g13)
    c: Equal(g29,g27)
    c: Diameter(g6) = 12.682  'diameter'
    c: DistanceX(g27,g27) = 1.90231
    c: PointOnObject(g22,g9)
    c: DistanceX(g7,g3) = 9
    c: Horizontal(g3,g7)
    c: Vertical(g19,g22)
FEATURE [PartDesign::Pocket] Pocket008  label="Hex"
  BaseFeature = -> Fillet
  Direction = (0,1,2e-16)
  Length = 6
  Length2 = 5
  Profile = -> Sketch021
  ReferenceAxis = -> Sketch021 [N_Axis]
  Reversed = true
  Suppressed = false
  Type = 0
FEATURE [PartDesign::LinearPattern] LinearPattern  label="HexAirVent"
  BaseFeature = -> Pocket008
  Direction = -> Sketch021 [H_Axis]
  Length = 100
  Mode = 0
  Occurrences = 9
  Offset = 12.5
  Originals = -> [Pocket008]
  Suppressed = false
  TransformMode = 0
FEATURE [Sketcher::SketchObject] Sketch022  label="BackOpeningSketch"
  ArcFitTolerance = 0
  AttachmentOffset = pos=(0,0,21) rot=(0,0,1;0rad)
  AttachmentSupport = -> [XZ_Plane001]
  FullyConstrained = true
  MakeInternals = false
  MapMode = 5
  Placement = pos=(0,-21,4.7e-15) rot=(1,0,0;1.5708rad)
  sketch-geometry (4):
    g0: LineSegment StartX=42.5 StartY=15 StartZ=0 EndX=-42.5 EndY=15 EndZ=0
    g1: LineSegment StartX=-42.5 StartY=15 StartZ=0 EndX=-42.5 EndY=120 EndZ=0
    g2: LineSegment StartX=-42.5 StartY=120 StartZ=0 EndX=42.5 EndY=120 EndZ=0
    g3: LineSegment StartX=42.5 StartY=120 StartZ=0 EndX=42.5 EndY=15 EndZ=0
  constraints (11):
    c: Coincident(g0,g1)
    c: Coincident(g1,g2)
    c: Coincident(g2,g3)
    c: Coincident(g3,g0)
    c: Horizontal(g2)
    c: Vertical(g1)
    c: Vertical(g3)
    c: DistanceY(g-1,g0) = 15
    c: Symmetric(g0,g0,g-2)
    c: DistanceX(g2,g2) = 85
    c: DistanceY(g3,g3) = 105
FEATURE [PartDesign::Pocket] Pocket009  label="BackOpening"
  BaseFeature = -> LinearPattern
  Direction = (0,1,2e-16)
  Length = 5
  Length2 = 5
  Profile = -> Sketch022
  ReferenceAxis = -> Sketch022 [N_Axis]
  Suppressed = false
  Type = 0
FEATURE [PartDesign::Body] Body001  label="ConnectorBody"
  AllowCompound = false
  Group = -> [Sketch005,Pad002,Sketch006,Pad003,Sketch007,Pocket003,Sketch008,Pad004,Pad009,Sketch010,Sketch011,Pocket005,Sketch014,Pocket007,Fillet,Sketch021,Pocket008,LinearPattern,Sketch022,Pocket009]
  Origin = -> Origin001
  Tip = -> Pocket009
FEATURE [PartDesign::Pocket] Pocket001  label="FanInntake"
  AlongSketchNormal = false
  BaseFeature = -> Pad001
  Direction = (0,1,-2e-16)
  Length = 5
  Length2 = 5
  Midplane = true
  Profile = -> Sketch003
  ReferenceAxis = -> Sketch003 [N_Axis]
  Suppressed = false
  Type = 0
FEATURE [PartDesign::Pocket] Pocket  label="FanSkrews"
  BaseFeature = -> Pocket001
  Direction = (0,1,-2e-16)
  Length = 4
  Length2 = 5
  Profile = -> Sketch002
  ReferenceAxis = -> Sketch002 [N_Axis]
  Suppressed = false
  Type = 0
FEATURE [PartDesign::AdditiveLoft] AdditiveLoft  label="ExhaustPipe"
  BaseFeature = -> Pocket
  Closed = false
  Profile = -> Pocket [Face5]
  Ruled = false
  Sections = -> [Sketch001]
  Suppressed = false
FEATURE [PartDesign::Pad] Pad
  BaseFeature = -> AdditiveLoft
  Direction = (0,0,1)
  Length = 30
  Length2 = 10
  Profile = -> AdditiveLoft [Face19]
  Suppressed = false
  Type = 0
FEATURE [PartDesign::Body] Body  label="FanBody"
  AllowCompound = false
  Group = -> [Sketch,Pad001,Sketch001,Sketch002,Sketch003,Pocket001,Pocket,AdditiveLoft,Pad]
  Origin = -> Origin
  Tip = -> Pad
FEATURE [Mesh::Feature] Mesh  label="ConnectorTap (Meshed)"
FEATURE [Mesh::Feature] Mesh001  label="BowdenAttachment (Meshed)"
